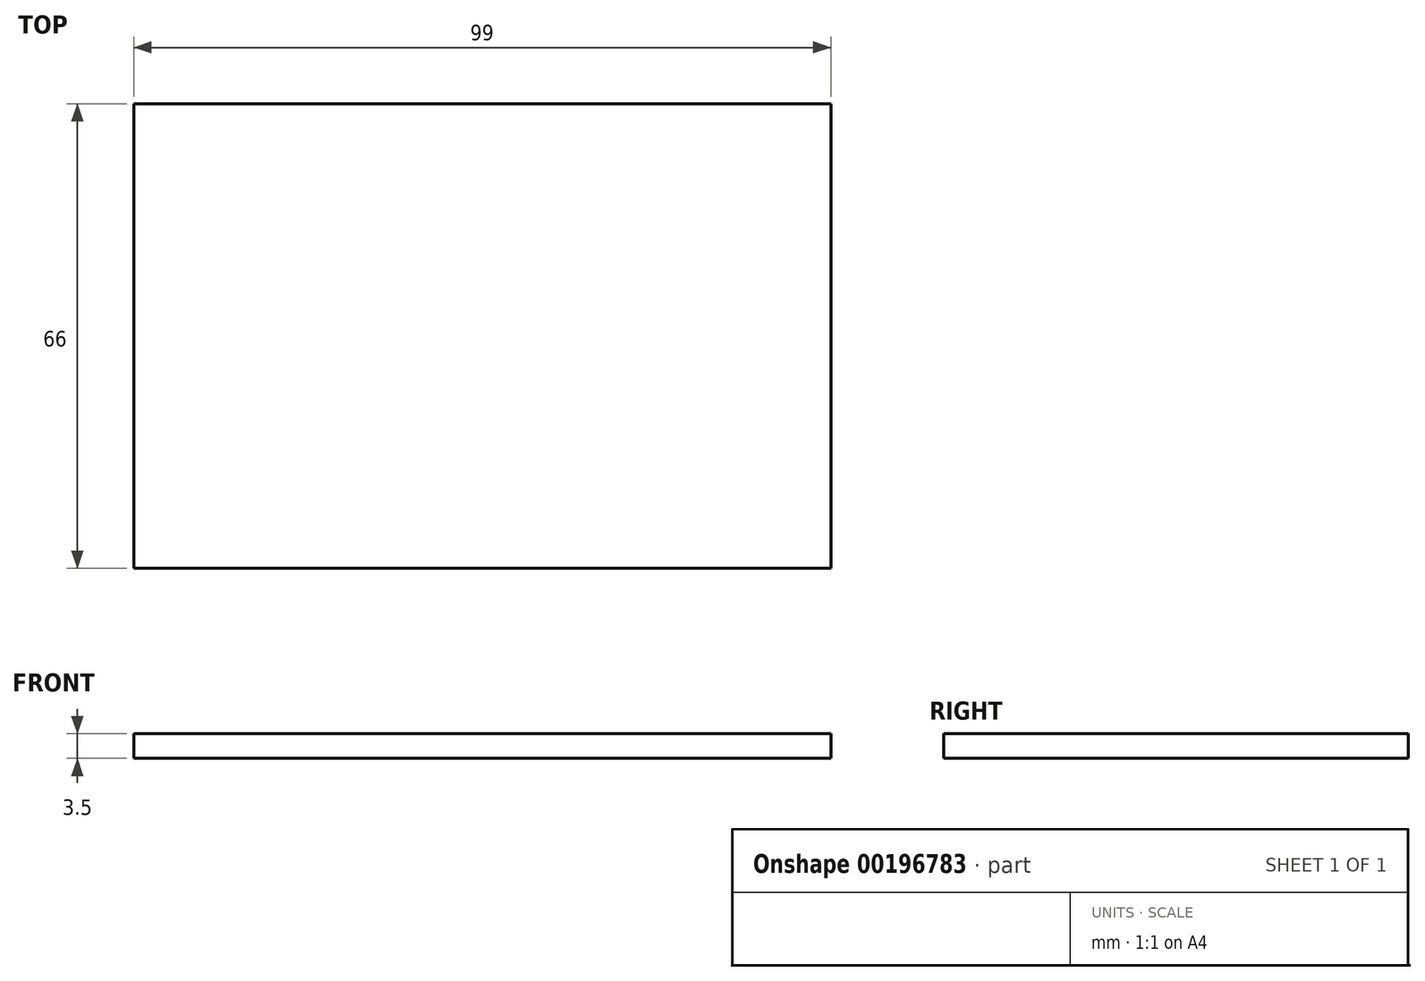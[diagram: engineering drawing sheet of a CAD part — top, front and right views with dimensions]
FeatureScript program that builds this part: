
annotation { "Feature Type Name" : "Feature", "Feature Type Description" : "" }
export const myFeature = defineFeature(function(context is Context, id is Id, definition is map)
    precondition{}
    {
        {
            var Q0;
            Q0=qCreatedBy(makeId("Top.planeOp"),FACE);
            var sketch = newSketch(context, id + "F0", { "sketchPlane" : qUnion([Q0])});
            skLineSegment(sketch, "E0.bottom", {"start": v(-49.5, -33) * mm, "end": v(49.5, -33) * mm});
            skLineSegment(sketch, "E0.top", {"start": v(-49.5, 33) * mm, "end": v(49.5, 33) * mm});
            skLineSegment(sketch, "E0.left", {"start": v(-49.5, -33) * mm, "end": v(-49.5, 33) * mm});
            skLineSegment(sketch, "E0.right", {"start": v(49.5, -33) * mm, "end": v(49.5, 33) * mm});
            skPoint(sketch, "E0.middle", {"position": v(0, 0) * mm});
            skSolve(sketch);
        }
        {
            var Q0;
            Q0=makeQuery(id+"F0.imprint","IMPRINT",FACE,{"disambiguationData":[TD([[makeQuery(id+"F0.imprint","IMPRINT",EDGE,{"derivedFrom":sQuery(id+"F0.wireOp",EDGE,"E0.bottom")}),1.0]])]});
            extrude(context, id + "F1", {"entities" : qUnion([Q0]), "depth" : 1.75 * mm, "hasSecondDirection" : true, "secondDirectionOppositeDirection" : true, "secondDirectionDepth" : 1.75 * mm});
        }
        {
            var Q0;
            Q0=qCreatedBy(makeId("Top.planeOp"),FACE);
            cPlane(context, id + "F2", {"entities" : qUnion([Q0]), "cplaneType" : CPlaneType.OFFSET, "offset" : 25 * mm, "width" : 150 * mm, "height" : 150 * mm});
        }
    });
